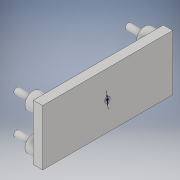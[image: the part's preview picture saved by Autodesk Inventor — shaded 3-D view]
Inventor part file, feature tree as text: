
AUTODESK INVENTOR PART (.ipt)
format: ipt  version: 2019 (Build 230136000, 136)  size: 171,008 bytes
history: native  units: mm
features: sketch x9, extrude x4, other x1, hole x1
ambient origin geometry x8: Origin, YZ Plane, XZ Plane, XY Plane, X Axis, Y Axis, Z Axis, Center Point
bodies: Body1 (feature_tree)
feature tree (15):
  other  "ソリッド1"
  sketch  "スケッチ1"
  extrude  "押し出し1"  Depth=60.0mm
  extrude  "押し出し2"  Depth=140.0mm
  sketch  "スケッチ4"
  sketch  "スケッチ5"
  extrude  "押し出し3"  Depth=10.0mm TaperAngle=0.0deg
  extrude  "押し出し4"  Depth=18.0mm
  sketch  "スケッチ7"
  sketch  "スケッチ8"
  hole  "穴1"  [1 undecoded]
  sketch  "スケッチ2"
  sketch  "スケッチ3"
  sketch  "スケッチ6"
  sketch  "スケッチ9"
note: 1 required parameter value undecoded (feature->parameter linkage not recoverable at this tier; creation-order binding heuristic only, values carry confidence <= 0.55)
